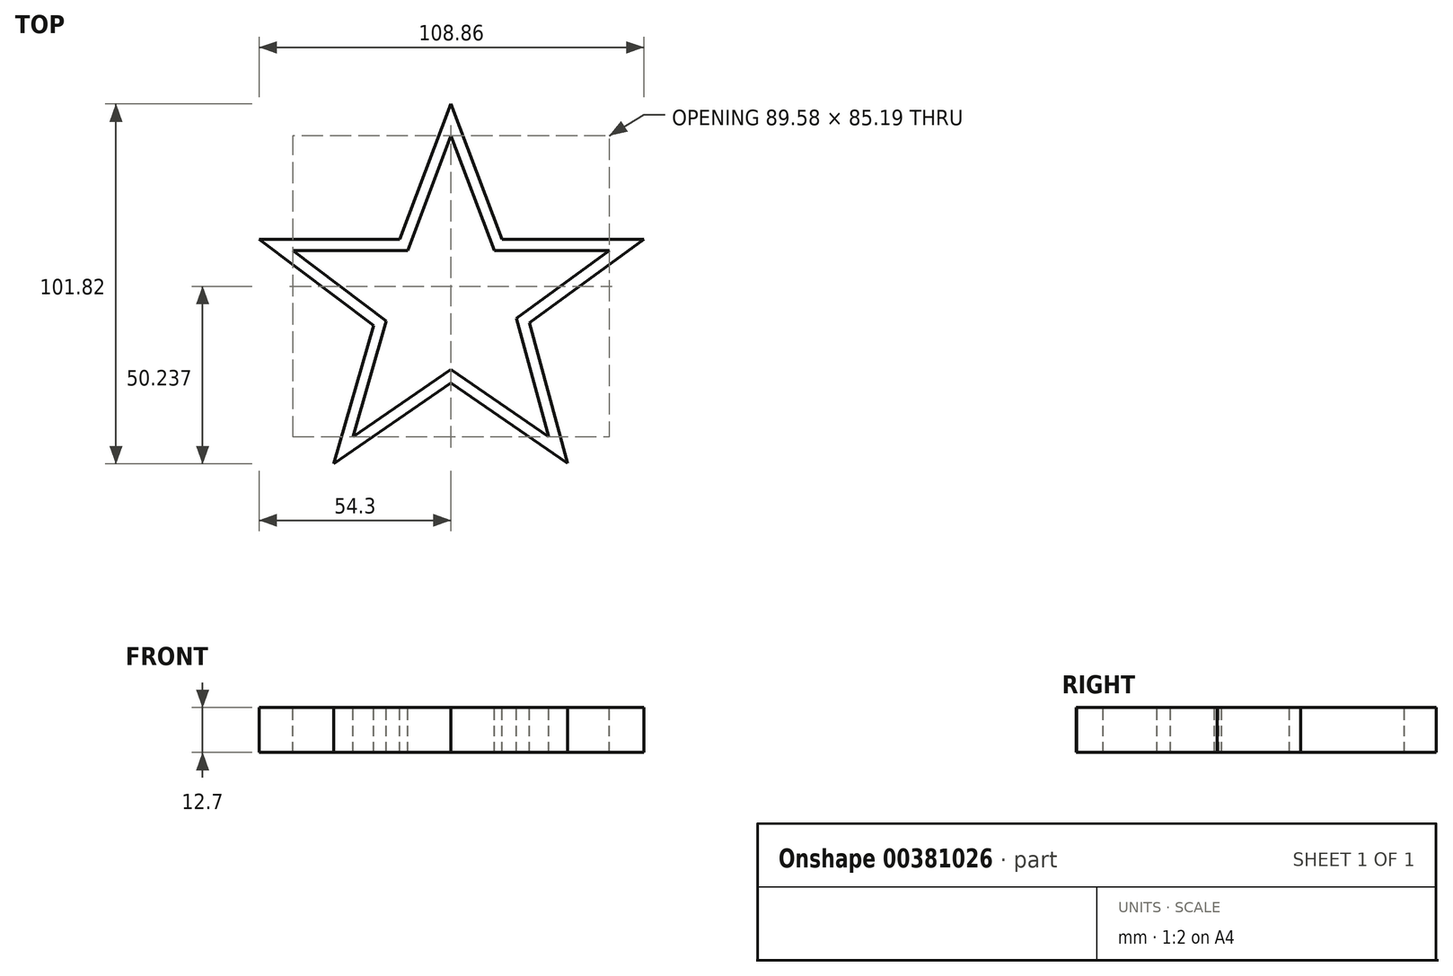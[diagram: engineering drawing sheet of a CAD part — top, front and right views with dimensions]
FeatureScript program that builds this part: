
annotation { "Feature Type Name" : "Feature", "Feature Type Description" : "" }
export const myFeature = defineFeature(function(context is Context, id is Id, definition is map)
    precondition{}
    {
        {
            var Q0;
            Q0=qCreatedBy(makeId("Top.planeOp"),FACE);
            var sketch = newSketch(context, id + "F0", { "sketchPlane" : qUnion([Q0])});
            skCircle(sketch, "E0.cCircle", {"center": v(0, 0) * mm, "radius": 38.1 * mm, "construction": true});
            skLineSegment(sketch, "E0.0", {"start": v(0, 47.1) * mm, "end": v(44.79, 14.55) * mm});
            skLineSegment(sketch, "E0.1", {"start": v(44.79, 14.55) * mm, "end": v(27.68, -38.1) * mm});
            skLineSegment(sketch, "E0.2", {"start": v(27.68, -38.1) * mm, "end": v(-27.68, -38.1) * mm});
            skLineSegment(sketch, "E0.3", {"start": v(-27.68, -38.1) * mm, "end": v(-44.79, 14.55) * mm});
            skLineSegment(sketch, "E0.4", {"start": v(-44.79, 14.55) * mm, "end": v(0, 47.1) * mm});
            skPoint(sketch, "E0.0.midPoint", {"position": v(22.4, 30.82) * mm});
            skCircle(sketch, "E1", {"center": v(0, 0) * mm, "radius": 19.05 * mm});
            skLineSegment(sketch, "E2", {"start": v(-27.68, -38.1) * mm, "end": v(0, -19.05) * mm});
            skLineSegment(sketch, "E3", {"start": v(0, -19.05) * mm, "end": v(27.68, -38.1) * mm});
            skLineSegment(sketch, "E4", {"start": v(44.79, 14.55) * mm, "end": v(12.3, 14.55) * mm});
            skLineSegment(sketch, "E5", {"start": v(-18.28, -5.36) * mm, "end": v(-44.79, 14.55) * mm});
            skLineSegment(sketch, "E6", {"start": v(-18.28, -5.36) * mm, "end": v(-27.68, -38.1) * mm});
            skLineSegment(sketch, "E7", {"start": v(44.79, 14.55) * mm, "end": v(18.5, -4.55) * mm});
            skLineSegment(sketch, "E8", {"start": v(18.5, -4.55) * mm, "end": v(27.68, -38.1) * mm});
            skLineSegment(sketch, "E9", {"start": v(12.3, 14.55) * mm, "end": v(0, 47.1) * mm});
            skLineSegment(sketch, "E10", {"start": v(0, 47.1) * mm, "end": v(-12.3, 14.55) * mm});
            skPoint(sketch, "E11", {"position": v(4.92, 18.4) * mm});
            skPoint(sketch, "E12", {"position": v(-12.3, 36.06) * mm});
            skPoint(sketch, "E13", {"position": v(-7.77, 37.3) * mm});
            skLineSegment(sketch, "E14.trimOffspring", {"start": v(-12.3, 14.55) * mm, "end": v(-44.79, 14.55) * mm});
            skLineSegment(sketch, "E15.0", {"start": v(54.56, 17.73) * mm, "end": v(14.49, 17.73) * mm});
            skLineSegment(sketch, "E15.1", {"start": v(54.56, 17.73) * mm, "end": v(22.14, -5.83) * mm});
            skLineSegment(sketch, "E15.2", {"start": v(14.49, 17.73) * mm, "end": v(0, 56.08) * mm});
            skLineSegment(sketch, "E15.3", {"start": v(22.14, -5.83) * mm, "end": v(33.04, -45.64) * mm});
            skLineSegment(sketch, "E15.4", {"start": v(0, -22.9) * mm, "end": v(33.04, -45.64) * mm});
            skLineSegment(sketch, "E15.5", {"start": v(-33.18, -45.74) * mm, "end": v(0, -22.9) * mm});
            skLineSegment(sketch, "E15.6", {"start": v(0, 56.08) * mm, "end": v(-14.49, 17.73) * mm});
            skLineSegment(sketch, "E15.7", {"start": v(-14.49, 17.73) * mm, "end": v(-54.3, 17.73) * mm});
            skLineSegment(sketch, "E15.8", {"start": v(-21.93, -6.59) * mm, "end": v(-54.3, 17.73) * mm});
            skLineSegment(sketch, "E15.9", {"start": v(-21.93, -6.59) * mm, "end": v(-33.18, -45.74) * mm});
            skSolve(sketch);
        }
        {
            var Q0;
            {var subQ3=sQuery(id+"F0.wireOp",EDGE,"E15.8");var subQ5=sQuery(id+"F0.wireOp",EDGE,"E15.7");var subQ7=makeQuery(id+"F0.imprint","INTERSECT",VERTEX,{"derivedFrom":[subQ5,subQ3]});Q0=makeQuery(id+"F0.imprint","IMPRINT",FACE,{"disambiguationData":[TD([[makeQuery(id+"F0.imprint","IMPRINT",EDGE,{"disambiguationData":[TD([[subQ7,1.0]])],"derivedFrom":subQ5}),1.0]])]});}
            var Q1;
            {var subQ0=sQuery(id+"F0.wireOp",EDGE,"E5");Q1=makeQuery(id+"F0.imprint","IMPRINT",FACE,{"disambiguationData":[TD([[makeQuery(id+"F0.imprint","IMPRINT",EDGE,{"derivedFrom":subQ0}),1.0]])]});}
            var Q2;
            {var subQ0=sQuery(id+"F0.wireOp",EDGE,"E10");Q2=makeQuery(id+"F0.imprint","IMPRINT",FACE,{"disambiguationData":[TD([[makeQuery(id+"F0.imprint","IMPRINT",EDGE,{"derivedFrom":subQ0}),-1.0]])]});}
            var Q3;
            {var subQ3=sQuery(id+"F0.wireOp",EDGE,"E15.2");var subQ5=sQuery(id+"F0.wireOp",EDGE,"E15.6");var subQ6=makeQuery(id+"F0.imprint","INTERSECT",VERTEX,{"derivedFrom":[subQ3,subQ5]});Q3=makeQuery(id+"F0.imprint","IMPRINT",FACE,{"disambiguationData":[TD([[makeQuery(id+"F0.imprint","IMPRINT",EDGE,{"disambiguationData":[TD([[subQ6,1.0]])],"derivedFrom":subQ3}),1.0]])]});}
            var Q4;
            {var subQ1=sQuery(id+"F0.wireOp",EDGE,"E4");Q4=makeQuery(id+"F0.imprint","IMPRINT",FACE,{"disambiguationData":[TD([[makeQuery(id+"F0.imprint","IMPRINT",EDGE,{"derivedFrom":subQ1}),-1.0]])]});}
            var Q5;
            {var subQ3=sQuery(id+"F0.wireOp",EDGE,"E15.0");var subQ5=sQuery(id+"F0.wireOp",EDGE,"E15.1");var subQ6=makeQuery(id+"F0.imprint","INTERSECT",VERTEX,{"derivedFrom":[subQ3,subQ5]});Q5=makeQuery(id+"F0.imprint","IMPRINT",FACE,{"disambiguationData":[TD([[makeQuery(id+"F0.imprint","IMPRINT",EDGE,{"disambiguationData":[TD([[subQ6,-1.0]])],"derivedFrom":subQ3}),1.0]])]});}
            var Q6;
            {var subQ1=sQuery(id+"F0.wireOp",EDGE,"E7");Q6=makeQuery(id+"F0.imprint","IMPRINT",FACE,{"disambiguationData":[TD([[makeQuery(id+"F0.imprint","IMPRINT",EDGE,{"derivedFrom":subQ1}),1.0]])]});}
            var Q7;
            {var subQ3=sQuery(id+"F0.wireOp",EDGE,"E15.3");var subQ5=sQuery(id+"F0.wireOp",EDGE,"E15.4");var subQ7=makeQuery(id+"F0.imprint","INTERSECT",VERTEX,{"derivedFrom":[subQ3,subQ5]});Q7=makeQuery(id+"F0.imprint","IMPRINT",FACE,{"disambiguationData":[TD([[makeQuery(id+"F0.imprint","IMPRINT",EDGE,{"disambiguationData":[TD([[subQ7,1.0]])],"derivedFrom":subQ3}),-1.0]])]});}
            var Q8;
            {var subQ0=sQuery(id+"F0.wireOp",EDGE,"E2");Q8=makeQuery(id+"F0.imprint","IMPRINT",FACE,{"disambiguationData":[TD([[makeQuery(id+"F0.imprint","IMPRINT",EDGE,{"derivedFrom":subQ0}),-1.0]])]});}
            var Q9;
            {var subQ3=sQuery(id+"F0.wireOp",EDGE,"E15.5");var subQ5=sQuery(id+"F0.wireOp",EDGE,"E15.9");var subQ7=makeQuery(id+"F0.imprint","INTERSECT",VERTEX,{"derivedFrom":[subQ3,subQ5]});Q9=makeQuery(id+"F0.imprint","IMPRINT",FACE,{"disambiguationData":[TD([[makeQuery(id+"F0.imprint","IMPRINT",EDGE,{"disambiguationData":[TD([[subQ7,-1.0]])],"derivedFrom":subQ3}),1.0]])]});}
            extrude(context, id + "F1", {"entities" : qUnion([Q0, Q1, Q2, Q3, Q4, Q5, Q6, Q7, Q8, Q9]), "endBound" : BoundingType.SYMMETRIC, "oppositeDirection" : true, "depth" : 12.7 * mm});
        }
    });
